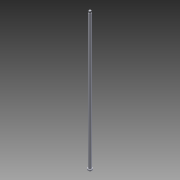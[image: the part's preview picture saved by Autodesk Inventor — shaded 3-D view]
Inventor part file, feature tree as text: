
AUTODESK INVENTOR PART (.ipt)
format: ipt  version: 2015 (Build 190159000, 159)  size: 93,696 bytes
history: native  units: mm
features: extrude x4, sketch x4, thread x1, chamfer x1
ambient origin geometry x8: Origin, YZ Plane, XZ Plane, XY Plane, X Axis, Y Axis, Z Axis, Center Point
bodies: 实体1 (feature_tree)
feature tree (10):
  extrude  "拉伸1"  Depth=5.0mm TaperAngle=0.0deg
  extrude  "拉伸2"  Depth=10.0mm TaperAngle=0.0deg
  extrude  "拉伸3"  Depth=2.0mm
  extrude  "拉伸4"  Depth=10.0mm
  thread  "螺纹2"  [1 undecoded]
  chamfer  "倒角2"  Distance=7.0mm
  sketch  "草图1"  dims[d0=15.0mm d1=5.0mm d2=0.0mm]
  sketch  "草图2"  dims[d3=10.0mm d4=490.0mm d5=0.0mm]
  sketch  "草图3"  dims[d6=2.0mm d7=2.0mm]
  sketch  "草图4"  dims[d8=485.0mm d9=0.0mm d15=8.0mm d16=10.0mm d17=7.0mm d18=0.0mm d19=10.0mm d20=0.0mm d21=0.25mm d22=2.0mm d23=45.0deg]
note: 1 required parameter value undecoded (feature->parameter linkage not recoverable at this tier; creation-order binding heuristic only, values carry confidence <= 0.55)
